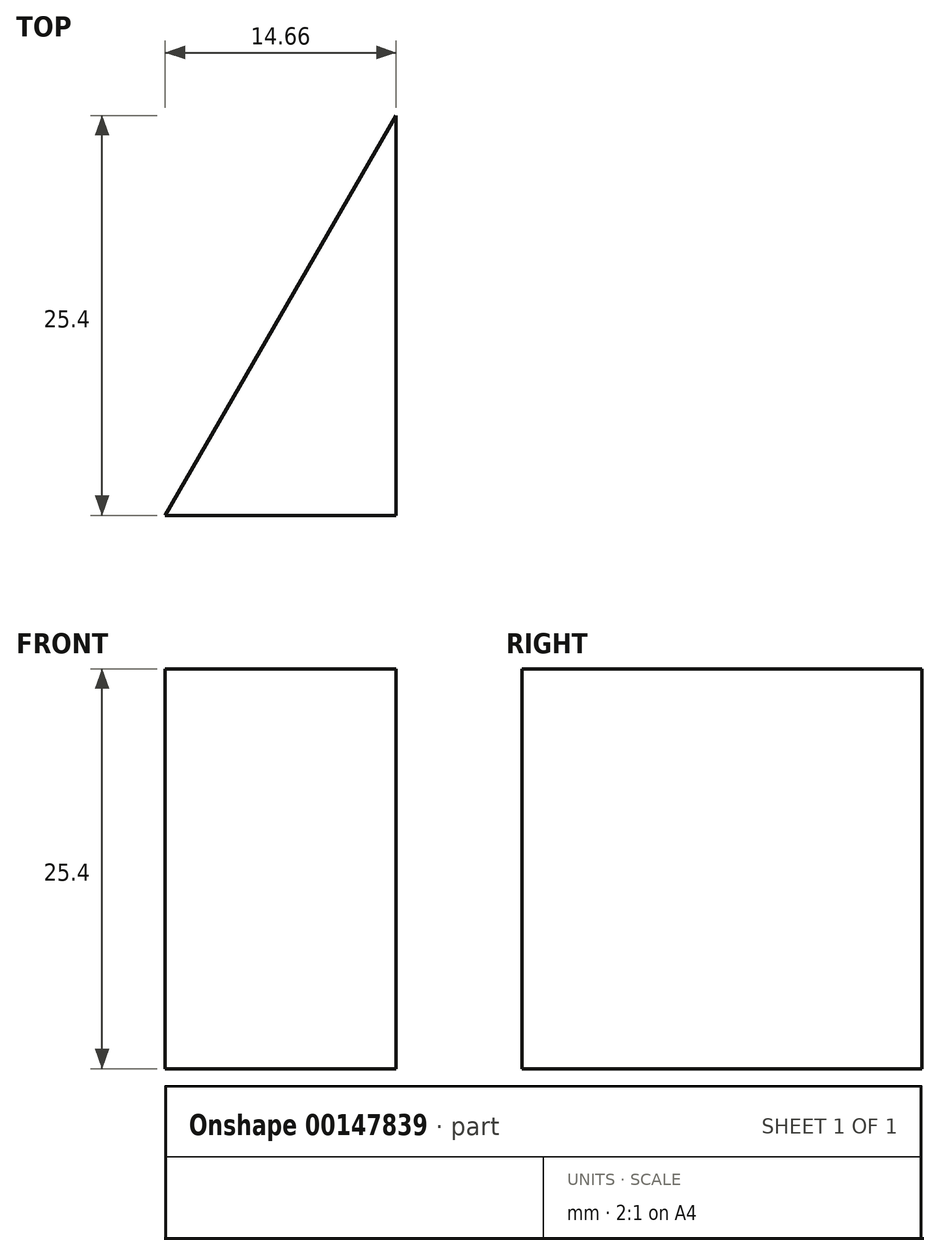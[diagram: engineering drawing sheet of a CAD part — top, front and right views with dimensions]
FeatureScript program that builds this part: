
annotation { "Feature Type Name" : "Feature", "Feature Type Description" : "" }
export const myFeature = defineFeature(function(context is Context, id is Id, definition is map)
    precondition{}
    {
        {
            var Q0;
            Q0=qCreatedBy(makeId("Top.planeOp"),FACE);
            var sketch = newSketch(context, id + "F0", { "sketchPlane" : qUnion([Q0])});
            skLineSegment(sketch, "E0.bottom", {"start": v(0, 0) * mm, "end": v(-14.66, 0) * mm});
            skLineSegment(sketch, "E0.left", {"start": v(0, 0) * mm, "end": v(0, 25.4) * mm});
            skLineSegment(sketch, "E1", {"start": v(-14.66, 0) * mm, "end": v(0, 25.4) * mm});
            skSolve(sketch);
        }
        {
            var Q0;
            Q0=makeQuery(id+"F0.imprint","IMPRINT",FACE,{"disambiguationData":[TD([[makeQuery(id+"F0.imprint","IMPRINT",EDGE,{"derivedFrom":sQuery(id+"F0.wireOp",EDGE,"E0.bottom")}),-1.0]])]});
            extrude(context, id + "F1", {"entities" : qUnion([Q0]), "depth" : 25.4 * mm});
        }
    });
